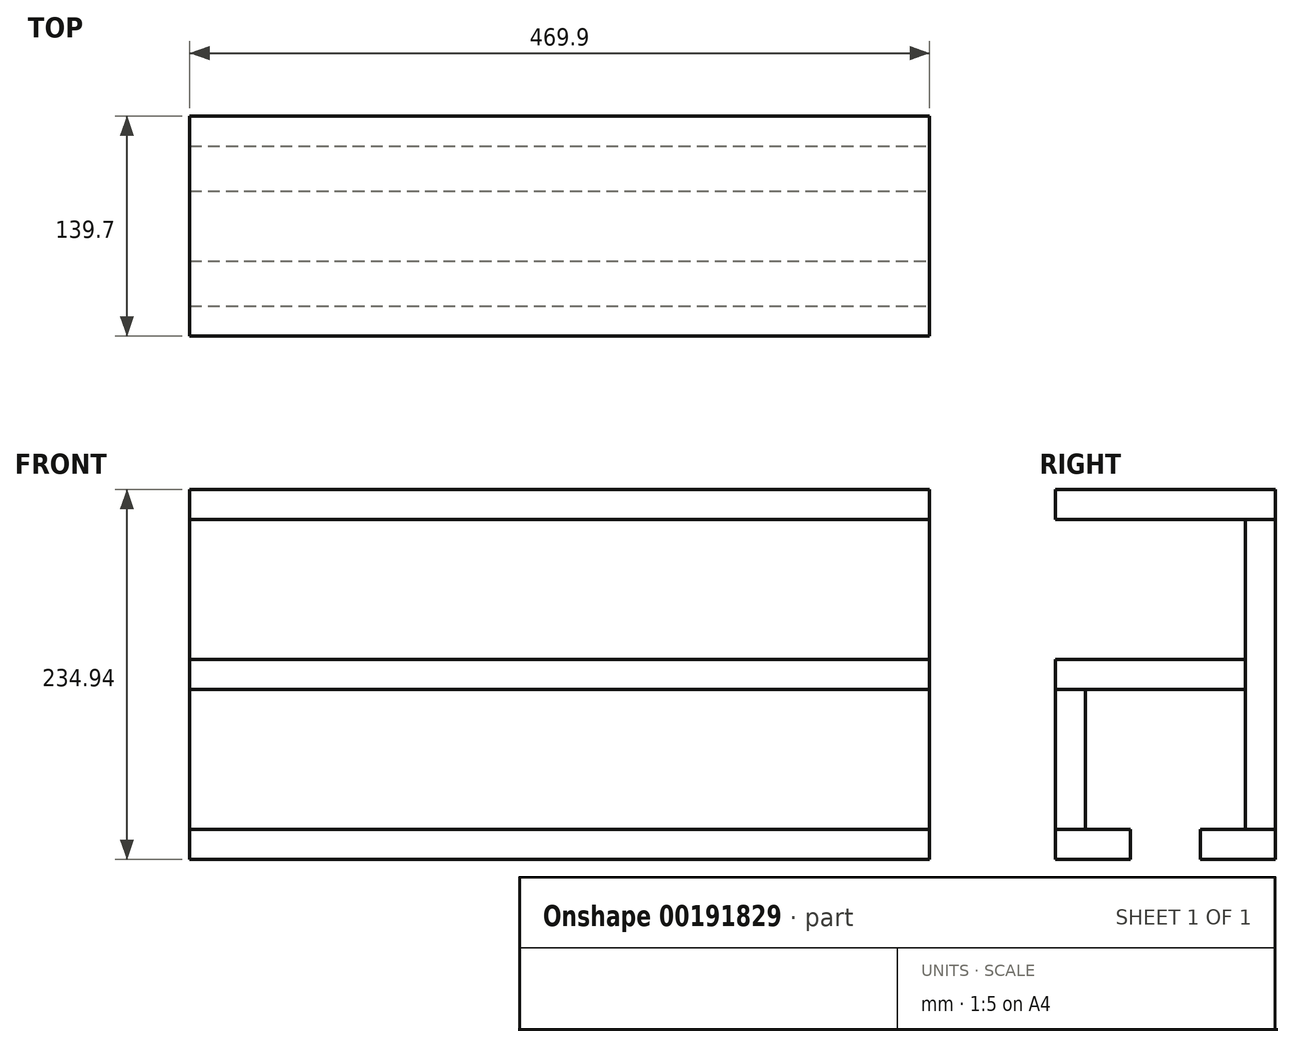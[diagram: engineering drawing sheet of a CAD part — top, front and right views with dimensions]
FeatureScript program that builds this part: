
annotation { "Feature Type Name" : "Feature", "Feature Type Description" : "" }
export const myFeature = defineFeature(function(context is Context, id is Id, definition is map)
    precondition{}
    {
        {
            var Q0;
            Q0=qCreatedBy(makeId("Front.planeOp"),FACE);
            var sketch = newSketch(context, id + "F0", { "sketchPlane" : qUnion([Q0])});
            skLineSegment(sketch, "E0.bottom", {"start": v(234.95, -98.42) * mm, "end": v(-234.95, -98.42) * mm});
            skLineSegment(sketch, "E0.top", {"start": v(234.95, 98.43) * mm, "end": v(-234.95, 98.43) * mm});
            skLineSegment(sketch, "E0.left", {"start": v(234.95, -98.42) * mm, "end": v(234.95, 98.43) * mm});
            skLineSegment(sketch, "E0.right", {"start": v(-234.95, -98.42) * mm, "end": v(-234.95, 98.43) * mm});
            skPoint(sketch, "E0.middle", {"position": v(0, 0) * mm});
            skSolve(sketch);
        }
        {
            var Q0;
            Q0=makeQuery(id+"F0.imprint","IMPRINT",FACE,{"disambiguationData":[TD([[makeQuery(id+"F0.imprint","IMPRINT",EDGE,{"derivedFrom":sQuery(id+"F0.wireOp",EDGE,"E0.bottom")}),-1.0]])]});
            extrude(context, id + "F1", {"entities" : qUnion([Q0]), "depth" : 19.05 * mm});
        }
        {
            var Q0;
            Q0=makeQuery(id+"F1.opExtrude","CAP_FACE",FACE,{"disambiguationData":[OSD([sQuery(id+"F0.wireOp",EDGE,"E0.bottom"),sQuery(id+"F0.wireOp",EDGE,"E0.top"),sQuery(id+"F0.wireOp",EDGE,"E0.left"),sQuery(id+"F0.wireOp",EDGE,"E0.right")])],"isStart":false});
            var sketch = newSketch(context, id + "F2", { "sketchPlane" : qUnion([Q0])});
            skLineSegment(sketch, "E1.bottom", {"start": v(-234.95, -9.53) * mm, "end": v(234.95, -9.52) * mm});
            skLineSegment(sketch, "E1.top", {"start": v(-234.95, 9.53) * mm, "end": v(234.95, 9.53) * mm});
            skLineSegment(sketch, "E1.left", {"start": v(-234.95, -9.53) * mm, "end": v(-234.95, 9.53) * mm});
            skLineSegment(sketch, "E1.right", {"start": v(234.95, -9.52) * mm, "end": v(234.95, 9.53) * mm});
            skSolve(sketch);
        }
        {
            var Q0;
            Q0 = qSketchRegion(id + "F2", true);
            extrude(context, id + "F3", {"entities" : qUnion([Q0]), "depth" : 120.65 * mm});
        }
        {
            var Q0;
            Q0=makeQuery(id+"F3.opExtrude","SWEPT_FACE",FACE,{"disambiguationData":[OSD([sQuery(id+"F2.wireOp",EDGE,"E1.bottom")])]});
            var sketch = newSketch(context, id + "F4", { "sketchPlane" : qUnion([Q0])});
            skLineSegment(sketch, "E2.bottom", {"start": v(-234.95, 139.7) * mm, "end": v(234.95, 139.7) * mm});
            skLineSegment(sketch, "E2.top", {"start": v(-234.95, 120.65) * mm, "end": v(234.95, 120.65) * mm});
            skLineSegment(sketch, "E2.left", {"start": v(-234.95, 139.7) * mm, "end": v(-234.95, 120.65) * mm});
            skLineSegment(sketch, "E2.right", {"start": v(234.95, 139.7) * mm, "end": v(234.95, 120.65) * mm});
            skSolve(sketch);
        }
        {
            var Q0;
            Q0 = qSketchRegion(id + "F4", true);
            extrude(context, id + "F5", {"entities" : qUnion([Q0]), "depth" : 88.9 * mm});
        }
        {
            var Q0;
            Q0=makeQuery(id+"F1.opExtrude","SWEPT_FACE",FACE,{"disambiguationData":[OSD([sQuery(id+"F0.wireOp",EDGE,"E0.bottom")])]});
            var sketch = newSketch(context, id + "F6", { "sketchPlane" : qUnion([Q0])});
            skLineSegment(sketch, "E3.bottom", {"start": v(-234.95, 0) * mm, "end": v(234.95, 0) * mm});
            skLineSegment(sketch, "E3.top", {"start": v(-234.95, 47.63) * mm, "end": v(234.95, 47.63) * mm});
            skLineSegment(sketch, "E3.left", {"start": v(-234.95, 0) * mm, "end": v(-234.95, 47.63) * mm});
            skLineSegment(sketch, "E3.right", {"start": v(234.95, 0) * mm, "end": v(234.95, 47.63) * mm});
            skSolve(sketch);
        }
        {
            var Q0;
            Q0 = qSketchRegion(id + "F6", true);
            extrude(context, id + "F7", {"entities" : qUnion([Q0]), "depth" : 19.05 * mm});
        }
        {
            var Q0;
            Q0=makeQuery(id+"F5.opExtrude","CAP_FACE",FACE,{"disambiguationData":[OSD([sQuery(id+"F4.wireOp",EDGE,"E2.bottom"),sQuery(id+"F4.wireOp",EDGE,"E2.top"),sQuery(id+"F4.wireOp",EDGE,"E2.left"),sQuery(id+"F4.wireOp",EDGE,"E2.right")])],"isStart":false});
            var sketch = newSketch(context, id + "F8", { "sketchPlane" : qUnion([Q0])});
            skLineSegment(sketch, "E4.bottom", {"start": v(-234.95, 139.7) * mm, "end": v(234.95, 139.7) * mm});
            skLineSegment(sketch, "E4.top", {"start": v(-234.95, 92.08) * mm, "end": v(234.95, 92.08) * mm});
            skLineSegment(sketch, "E4.left", {"start": v(-234.95, 139.7) * mm, "end": v(-234.95, 92.08) * mm});
            skLineSegment(sketch, "E4.right", {"start": v(234.95, 139.7) * mm, "end": v(234.95, 92.08) * mm});
            skSolve(sketch);
        }
        {
            var Q0;
            Q0 = qSketchRegion(id + "F8", true);
            extrude(context, id + "F9", {"entities" : qUnion([Q0]), "depth" : 19.05 * mm});
        }
        {
            var Q0;
            Q0=makeQuery(id+"F1.opExtrude","SWEPT_FACE",FACE,{"disambiguationData":[OSD([sQuery(id+"F0.wireOp",EDGE,"E0.top")])]});
            var sketch = newSketch(context, id + "F10", { "sketchPlane" : qUnion([Q0])});
            skLineSegment(sketch, "E5.bottom", {"start": v(-234.95, 0) * mm, "end": v(234.95, 0) * mm});
            skLineSegment(sketch, "E5.top", {"start": v(-234.95, -139.7) * mm, "end": v(234.95, -139.7) * mm});
            skLineSegment(sketch, "E5.left", {"start": v(-234.95, 0) * mm, "end": v(-234.95, -139.7) * mm});
            skLineSegment(sketch, "E5.right", {"start": v(234.95, 0) * mm, "end": v(234.95, -139.7) * mm});
            skSolve(sketch);
        }
        {
            var Q0;
            Q0 = qSketchRegion(id + "F10", true);
            extrude(context, id + "F11", {"entities" : qUnion([Q0]), "depth" : 19.05 * mm});
        }
    });
